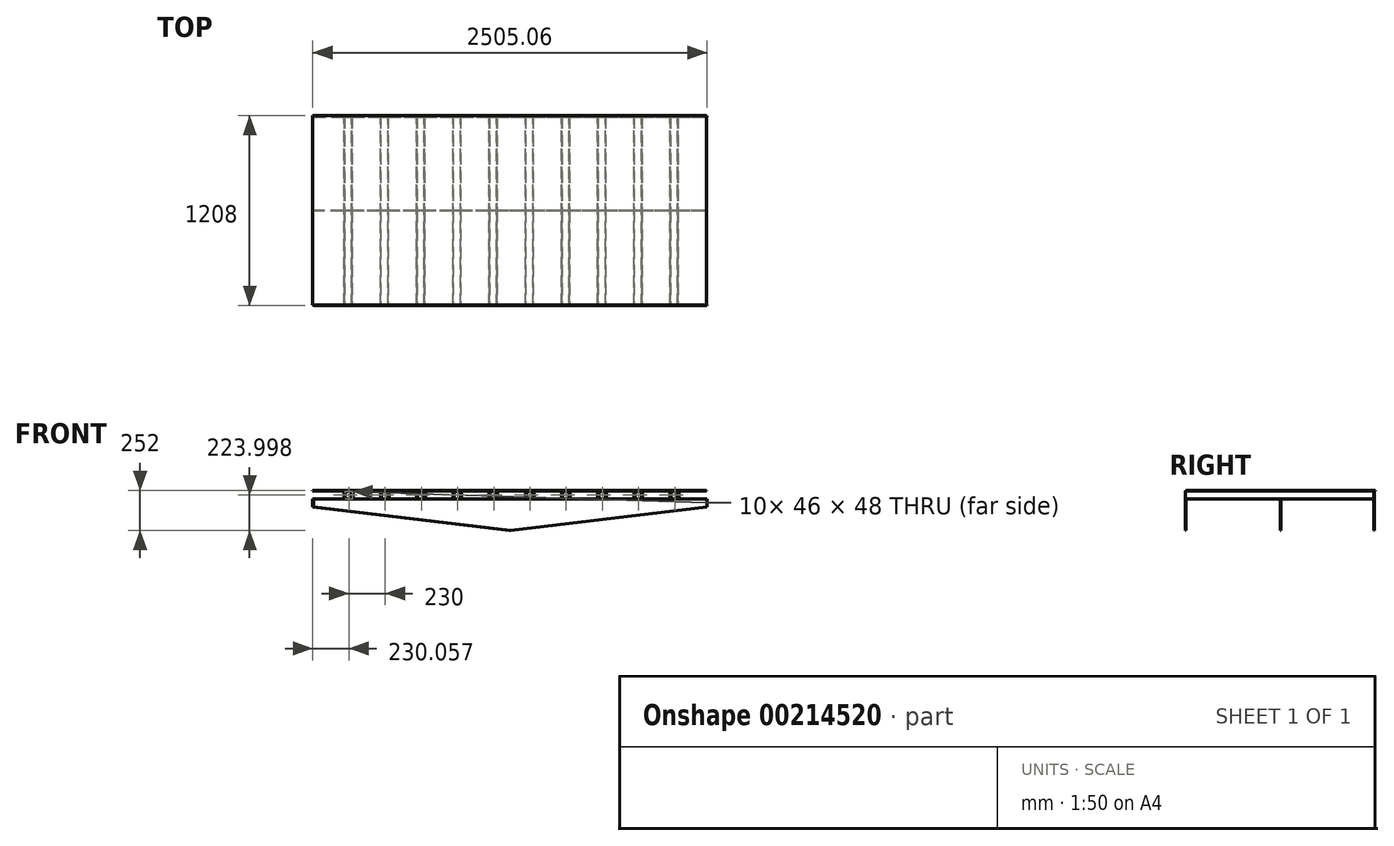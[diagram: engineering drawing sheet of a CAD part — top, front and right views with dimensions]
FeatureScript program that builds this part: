
annotation { "Feature Type Name" : "Feature", "Feature Type Description" : "" }
export const myFeature = defineFeature(function(context is Context, id is Id, definition is map)
    precondition{}
    {
        {
            var Q0;
            Q0=qCreatedBy(makeId("Front.planeOp"),FACE);
            var sketch = newSketch(context, id + "F0", { "sketchPlane" : qUnion([Q0])});
            skLineSegment(sketch, "E0.bottom", {"start": v(-1251.25, 23.13) * mm, "end": v(1248.75, 23.13) * mm});
            skLineSegment(sketch, "E1.bottom", {"start": v(-1051.25, 73.13) * mm, "end": v(-1001.25, 73.13) * mm});
            skLineSegment(sketch, "E1.left", {"start": v(-1001.25, 73.13) * mm, "end": v(-1001.25, 23.13) * mm});
            skLineSegment(sketch, "E1.right", {"start": v(-1051.25, 73.13) * mm, "end": v(-1051.25, 23.13) * mm});
            skLineSegment(sketch, "E2", {"start": v(-1251.25, 23.13) * mm, "end": v(-1251.25, -26.87) * mm});
            skLineSegment(sketch, "E3", {"start": v(-1251.25, -26.87) * mm, "end": v(0, -176.87) * mm});
            skLineSegment(sketch, "E4", {"start": v(0, -176.87) * mm, "end": v(1248.75, -26.87) * mm});
            skLineSegment(sketch, "E5", {"start": v(1248.75, -26.87) * mm, "end": v(1248.75, 23.13) * mm});
            skLineSegment(sketch, "E6", {"start": v(-1003.25, 23.13) * mm, "end": v(-1003.25, 71.13) * mm});
            skLineSegment(sketch, "E7", {"start": v(-1003.25, 71.13) * mm, "end": v(-1049.25, 71.13) * mm});
            skLineSegment(sketch, "E8", {"start": v(-1049.25, 71.13) * mm, "end": v(-1049.25, 23.13) * mm});
            skLineSegment(sketch, "E9.1.0.0", {"start": v(-821.25, 73.13) * mm, "end": v(-821.25, 23.13) * mm});
            skLineSegment(sketch, "E9.1.0.1", {"start": v(-773.25, 23.13) * mm, "end": v(-773.25, 71.13) * mm});
            skLineSegment(sketch, "E9.1.0.2", {"start": v(-821.25, 73.13) * mm, "end": v(-771.25, 73.13) * mm});
            skLineSegment(sketch, "E9.1.0.3", {"start": v(-771.25, 73.13) * mm, "end": v(-771.25, 23.13) * mm});
            skLineSegment(sketch, "E9.1.0.4", {"start": v(-773.25, 71.13) * mm, "end": v(-819.25, 71.13) * mm});
            skLineSegment(sketch, "E9.1.0.5", {"start": v(-819.25, 71.13) * mm, "end": v(-819.25, 23.13) * mm});
            skLineSegment(sketch, "E9.2.0.0", {"start": v(-591.25, 73.13) * mm, "end": v(-591.25, 23.13) * mm});
            skLineSegment(sketch, "E9.2.0.1", {"start": v(-543.25, 23.13) * mm, "end": v(-543.25, 71.13) * mm});
            skLineSegment(sketch, "E9.2.0.2", {"start": v(-591.25, 73.13) * mm, "end": v(-541.25, 73.13) * mm});
            skLineSegment(sketch, "E9.2.0.3", {"start": v(-541.25, 73.13) * mm, "end": v(-541.25, 23.13) * mm});
            skLineSegment(sketch, "E9.2.0.4", {"start": v(-543.25, 71.13) * mm, "end": v(-589.25, 71.13) * mm});
            skLineSegment(sketch, "E9.2.0.5", {"start": v(-589.25, 71.13) * mm, "end": v(-589.25, 23.13) * mm});
            skLineSegment(sketch, "E9.3.0.0", {"start": v(-361.25, 73.13) * mm, "end": v(-361.25, 23.13) * mm});
            skLineSegment(sketch, "E9.3.0.1", {"start": v(-313.25, 23.13) * mm, "end": v(-313.25, 71.13) * mm});
            skLineSegment(sketch, "E9.3.0.2", {"start": v(-361.25, 73.13) * mm, "end": v(-311.25, 73.13) * mm});
            skLineSegment(sketch, "E9.3.0.3", {"start": v(-311.25, 73.13) * mm, "end": v(-311.25, 23.13) * mm});
            skLineSegment(sketch, "E9.3.0.4", {"start": v(-313.25, 71.13) * mm, "end": v(-359.25, 71.13) * mm});
            skLineSegment(sketch, "E9.3.0.5", {"start": v(-359.25, 71.13) * mm, "end": v(-359.25, 23.13) * mm});
            skLineSegment(sketch, "E9.4.0.0", {"start": v(-131.25, 73.13) * mm, "end": v(-131.25, 23.13) * mm});
            skLineSegment(sketch, "E9.4.0.1", {"start": v(-83.25, 23.13) * mm, "end": v(-83.25, 71.13) * mm});
            skLineSegment(sketch, "E9.4.0.2", {"start": v(-131.25, 73.13) * mm, "end": v(-81.25, 73.13) * mm});
            skLineSegment(sketch, "E9.4.0.3", {"start": v(-81.25, 73.13) * mm, "end": v(-81.25, 23.13) * mm});
            skLineSegment(sketch, "E9.4.0.4", {"start": v(-83.25, 71.13) * mm, "end": v(-129.25, 71.13) * mm});
            skLineSegment(sketch, "E9.4.0.5", {"start": v(-129.25, 71.13) * mm, "end": v(-129.25, 23.13) * mm});
            skLineSegment(sketch, "E9.5.0.0", {"start": v(98.75, 73.13) * mm, "end": v(98.75, 23.13) * mm});
            skLineSegment(sketch, "E9.5.0.1", {"start": v(146.75, 23.13) * mm, "end": v(146.75, 71.13) * mm});
            skLineSegment(sketch, "E9.5.0.2", {"start": v(98.75, 73.13) * mm, "end": v(148.75, 73.13) * mm});
            skLineSegment(sketch, "E9.5.0.3", {"start": v(148.75, 73.13) * mm, "end": v(148.75, 23.13) * mm});
            skLineSegment(sketch, "E9.5.0.4", {"start": v(146.75, 71.13) * mm, "end": v(100.75, 71.13) * mm});
            skLineSegment(sketch, "E9.5.0.5", {"start": v(100.75, 71.13) * mm, "end": v(100.75, 23.13) * mm});
            skLineSegment(sketch, "E9.6.0.0", {"start": v(328.75, 73.13) * mm, "end": v(328.75, 23.13) * mm});
            skLineSegment(sketch, "E9.6.0.1", {"start": v(376.75, 23.13) * mm, "end": v(376.75, 71.13) * mm});
            skLineSegment(sketch, "E9.6.0.2", {"start": v(328.75, 73.13) * mm, "end": v(378.75, 73.13) * mm});
            skLineSegment(sketch, "E9.6.0.3", {"start": v(378.75, 73.13) * mm, "end": v(378.75, 23.13) * mm});
            skLineSegment(sketch, "E9.6.0.4", {"start": v(376.75, 71.13) * mm, "end": v(330.75, 71.13) * mm});
            skLineSegment(sketch, "E9.6.0.5", {"start": v(330.75, 71.13) * mm, "end": v(330.75, 23.13) * mm});
            skLineSegment(sketch, "E9.7.0.0", {"start": v(558.75, 73.13) * mm, "end": v(558.75, 23.13) * mm});
            skLineSegment(sketch, "E9.7.0.1", {"start": v(606.75, 23.13) * mm, "end": v(606.75, 71.13) * mm});
            skLineSegment(sketch, "E9.7.0.2", {"start": v(558.75, 73.13) * mm, "end": v(608.75, 73.13) * mm});
            skLineSegment(sketch, "E9.7.0.3", {"start": v(608.75, 73.13) * mm, "end": v(608.75, 23.13) * mm});
            skLineSegment(sketch, "E9.7.0.4", {"start": v(606.75, 71.13) * mm, "end": v(560.75, 71.13) * mm});
            skLineSegment(sketch, "E9.7.0.5", {"start": v(560.75, 71.13) * mm, "end": v(560.75, 23.13) * mm});
            skLineSegment(sketch, "E9.8.0.0", {"start": v(788.75, 73.13) * mm, "end": v(788.75, 23.13) * mm});
            skLineSegment(sketch, "E9.8.0.1", {"start": v(836.75, 23.13) * mm, "end": v(836.75, 71.13) * mm});
            skLineSegment(sketch, "E9.8.0.2", {"start": v(788.75, 73.13) * mm, "end": v(838.75, 73.13) * mm});
            skLineSegment(sketch, "E9.8.0.3", {"start": v(838.75, 73.13) * mm, "end": v(838.75, 23.13) * mm});
            skLineSegment(sketch, "E9.8.0.4", {"start": v(836.75, 71.13) * mm, "end": v(790.75, 71.13) * mm});
            skLineSegment(sketch, "E9.8.0.5", {"start": v(790.75, 71.13) * mm, "end": v(790.75, 23.13) * mm});
            skLineSegment(sketch, "E9.9.0.0", {"start": v(1018.75, 73.13) * mm, "end": v(1018.75, 23.13) * mm});
            skLineSegment(sketch, "E9.9.0.1", {"start": v(1066.75, 23.13) * mm, "end": v(1066.75, 71.13) * mm});
            skLineSegment(sketch, "E9.9.0.2", {"start": v(1018.75, 73.13) * mm, "end": v(1068.75, 73.13) * mm});
            skLineSegment(sketch, "E9.9.0.3", {"start": v(1068.75, 73.13) * mm, "end": v(1068.75, 23.13) * mm});
            skLineSegment(sketch, "E9.9.0.4", {"start": v(1066.75, 71.13) * mm, "end": v(1020.75, 71.13) * mm});
            skLineSegment(sketch, "E9.9.0.5", {"start": v(1020.75, 71.13) * mm, "end": v(1020.75, 23.13) * mm});
            skLineSegment(sketch, "E9.direction1", {"start": v(-1051.25, 23.13) * mm, "end": v(-821.25, 23.13) * mm, "construction": true});
            skSolve(sketch);
        }
        {
            var Q0;
            Q0 = qSketchRegion(id + "F0", true);
            extrude(context, id + "F1", {"entities" : qUnion([Q0]), "depth" : 5 * mm, "offsetDistance" : 25 * mm});
        }
        {
            var Q0;
            Q0=makeQuery(id+"F1.opExtrude","SWEPT_FACE",FACE,{"disambiguationData":[OSD([sQuery(id+"F0.wireOp",EDGE,"E1.bottom")])]});
            var sketch = newSketch(context, id + "F2", { "sketchPlane" : qUnion([Q0])});
            skLineSegment(sketch, "E10.bottom", {"start": v(-1251.25, 600) * mm, "end": v(1248.75, 600) * mm});
            skLineSegment(sketch, "E10.top", {"start": v(-1251.25, -605) * mm, "end": v(1248.75, -605) * mm});
            skLineSegment(sketch, "E10.left", {"start": v(-1251.25, 600) * mm, "end": v(-1251.25, -605) * mm});
            skLineSegment(sketch, "E10.right", {"start": v(1248.75, 600) * mm, "end": v(1248.75, -605) * mm});
            skSolve(sketch);
        }
        {
            var Q0;
            Q0 = qSketchRegion(id + "F2", true);
            extrude(context, id + "F3", {"entities" : qUnion([Q0]), "operationType" : NewBodyOperationType.ADD, "depth" : 2 * mm, "offsetDistance" : 25 * mm});
        }
        {
            var Q0;
            Q0=makeQuery(id+"F1.opExtrude","CAP_FACE",FACE,{"disambiguationData":[OSD([sQuery(id+"F0.wireOp",EDGE,"E0.bottom"),sQuery(id+"F0.wireOp",EDGE,"E1.bottom"),sQuery(id+"F0.wireOp",EDGE,"E1.left"),sQuery(id+"F0.wireOp",EDGE,"E1.right"),sQuery(id+"F0.wireOp",EDGE,"E2"),sQuery(id+"F0.wireOp",EDGE,"E3"),sQuery(id+"F0.wireOp",EDGE,"E4"),sQuery(id+"F0.wireOp",EDGE,"E5"),sQuery(id+"F0.wireOp",EDGE,"E6"),sQuery(id+"F0.wireOp",EDGE,"E7"),sQuery(id+"F0.wireOp",EDGE,"E8"),sQuery(id+"F0.wireOp",EDGE,"E9.1.0.0"),sQuery(id+"F0.wireOp",EDGE,"E9.1.0.1"),sQuery(id+"F0.wireOp",EDGE,"E9.1.0.2"),sQuery(id+"F0.wireOp",EDGE,"E9.1.0.3"),sQuery(id+"F0.wireOp",EDGE,"E9.1.0.4"),sQuery(id+"F0.wireOp",EDGE,"E9.1.0.5"),sQuery(id+"F0.wireOp",EDGE,"E9.2.0.0"),sQuery(id+"F0.wireOp",EDGE,"E9.2.0.1"),sQuery(id+"F0.wireOp",EDGE,"E9.2.0.2"),sQuery(id+"F0.wireOp",EDGE,"E9.2.0.3"),sQuery(id+"F0.wireOp",EDGE,"E9.2.0.4"),sQuery(id+"F0.wireOp",EDGE,"E9.2.0.5"),sQuery(id+"F0.wireOp",EDGE,"E9.3.0.0"),sQuery(id+"F0.wireOp",EDGE,"E9.3.0.1"),sQuery(id+"F0.wireOp",EDGE,"E9.3.0.2"),sQuery(id+"F0.wireOp",EDGE,"E9.3.0.3"),sQuery(id+"F0.wireOp",EDGE,"E9.3.0.4"),sQuery(id+"F0.wireOp",EDGE,"E9.3.0.5"),sQuery(id+"F0.wireOp",EDGE,"E9.4.0.0"),sQuery(id+"F0.wireOp",EDGE,"E9.4.0.1"),sQuery(id+"F0.wireOp",EDGE,"E9.4.0.2"),sQuery(id+"F0.wireOp",EDGE,"E9.4.0.3"),sQuery(id+"F0.wireOp",EDGE,"E9.4.0.4"),sQuery(id+"F0.wireOp",EDGE,"E9.4.0.5"),sQuery(id+"F0.wireOp",EDGE,"E9.5.0.0"),sQuery(id+"F0.wireOp",EDGE,"E9.5.0.1"),sQuery(id+"F0.wireOp",EDGE,"E9.5.0.2"),sQuery(id+"F0.wireOp",EDGE,"E9.5.0.3"),sQuery(id+"F0.wireOp",EDGE,"E9.5.0.4"),sQuery(id+"F0.wireOp",EDGE,"E9.5.0.5"),sQuery(id+"F0.wireOp",EDGE,"E9.6.0.0"),sQuery(id+"F0.wireOp",EDGE,"E9.6.0.1"),sQuery(id+"F0.wireOp",EDGE,"E9.6.0.2"),sQuery(id+"F0.wireOp",EDGE,"E9.6.0.3"),sQuery(id+"F0.wireOp",EDGE,"E9.6.0.4"),sQuery(id+"F0.wireOp",EDGE,"E9.6.0.5"),sQuery(id+"F0.wireOp",EDGE,"E9.7.0.0"),sQuery(id+"F0.wireOp",EDGE,"E9.7.0.1"),sQuery(id+"F0.wireOp",EDGE,"E9.7.0.2"),sQuery(id+"F0.wireOp",EDGE,"E9.7.0.3"),sQuery(id+"F0.wireOp",EDGE,"E9.7.0.4"),sQuery(id+"F0.wireOp",EDGE,"E9.7.0.5"),sQuery(id+"F0.wireOp",EDGE,"E9.8.0.0"),sQuery(id+"F0.wireOp",EDGE,"E9.8.0.1"),sQuery(id+"F0.wireOp",EDGE,"E9.8.0.2"),sQuery(id+"F0.wireOp",EDGE,"E9.8.0.3"),sQuery(id+"F0.wireOp",EDGE,"E9.8.0.4"),sQuery(id+"F0.wireOp",EDGE,"E9.8.0.5"),sQuery(id+"F0.wireOp",EDGE,"E9.9.0.0"),sQuery(id+"F0.wireOp",EDGE,"E9.9.0.1"),sQuery(id+"F0.wireOp",EDGE,"E9.9.0.2"),sQuery(id+"F0.wireOp",EDGE,"E9.9.0.3"),sQuery(id+"F0.wireOp",EDGE,"E9.9.0.4"),sQuery(id+"F0.wireOp",EDGE,"E9.9.0.5")])],"isStart":false});
            var sketch = newSketch(context, id + "F4", { "sketchPlane" : qUnion([Q0])});
            skSolve(sketch);
        }
        {
            var Q0;
            {var subQ21=sQuery(id+"F0.wireOp",EDGE,"E1.left");Q0=makeQuery(id+"F4.imprint","IMPRINT",FACE,{"disambiguationData":[TD([[makeQuery(id+"F4.imprint","IMPRINT",EDGE,{"derivedFrom":makeQuery(id+"F1.opExtrude","CAP_EDGE",EDGE,{"disambiguationData":[OSD([subQ21])],"isStart":false})}),-1.0]])]});}
            cPlane(context, id + "F5", {"entities" : qUnion([Q0]), "cplaneType" : CPlaneType.OFFSET, "offset" : 600 * mm, "width" : 150 * mm, "height" : 150 * mm});
        }
        {
            var Q0;
            Q0=qCreatedBy(id+"F5.planeOp",FACE);
            var sketch = newSketch(context, id + "F6", { "sketchPlane" : qUnion([Q0])});
            skLineSegment(sketch, "E11.bottom", {"start": v(-1246.2, 23.13) * mm, "end": v(1253.8, 23.13) * mm});
            skLineSegment(sketch, "E12.bottom", {"start": v(-1051.25, 73.13) * mm, "end": v(-1001.25, 73.13) * mm});
            skLineSegment(sketch, "E12.left", {"start": v(-1001.25, 73.13) * mm, "end": v(-1001.25, 23.13) * mm});
            skLineSegment(sketch, "E12.right", {"start": v(-1051.25, 73.13) * mm, "end": v(-1051.25, 23.13) * mm});
            skLineSegment(sketch, "E13", {"start": v(-1246.2, 23.13) * mm, "end": v(-1246.2, -26.87) * mm});
            skLineSegment(sketch, "E14", {"start": v(-1246.2, -26.87) * mm, "end": v(5.06, -176.87) * mm});
            skLineSegment(sketch, "E15", {"start": v(5.06, -176.87) * mm, "end": v(1253.8, -26.87) * mm});
            skLineSegment(sketch, "E16", {"start": v(1253.8, -26.87) * mm, "end": v(1253.8, 23.13) * mm});
            skLineSegment(sketch, "E17", {"start": v(-1003.25, 23.13) * mm, "end": v(-1003.25, 71.13) * mm});
            skLineSegment(sketch, "E18", {"start": v(-1003.25, 71.13) * mm, "end": v(-1049.25, 71.13) * mm});
            skLineSegment(sketch, "E19", {"start": v(-1049.25, 71.13) * mm, "end": v(-1049.25, 23.13) * mm});
            skLineSegment(sketch, "E20.1.0.0", {"start": v(-821.25, 73.13) * mm, "end": v(-821.25, 23.13) * mm});
            skLineSegment(sketch, "E20.1.0.1", {"start": v(-773.25, 23.13) * mm, "end": v(-773.25, 71.13) * mm});
            skLineSegment(sketch, "E20.1.0.2", {"start": v(-821.25, 73.13) * mm, "end": v(-771.25, 73.13) * mm});
            skLineSegment(sketch, "E20.1.0.3", {"start": v(-771.25, 73.13) * mm, "end": v(-771.25, 23.13) * mm});
            skLineSegment(sketch, "E20.1.0.4", {"start": v(-773.25, 71.13) * mm, "end": v(-819.25, 71.13) * mm});
            skLineSegment(sketch, "E20.1.0.5", {"start": v(-819.25, 71.13) * mm, "end": v(-819.25, 23.13) * mm});
            skLineSegment(sketch, "E20.2.0.0", {"start": v(-591.25, 73.13) * mm, "end": v(-591.25, 23.13) * mm});
            skLineSegment(sketch, "E20.2.0.1", {"start": v(-543.25, 23.13) * mm, "end": v(-543.25, 71.13) * mm});
            skLineSegment(sketch, "E20.2.0.2", {"start": v(-591.25, 73.13) * mm, "end": v(-541.25, 73.13) * mm});
            skLineSegment(sketch, "E20.2.0.3", {"start": v(-541.25, 73.13) * mm, "end": v(-541.25, 23.13) * mm});
            skLineSegment(sketch, "E20.2.0.4", {"start": v(-543.25, 71.13) * mm, "end": v(-589.25, 71.13) * mm});
            skLineSegment(sketch, "E20.2.0.5", {"start": v(-589.25, 71.13) * mm, "end": v(-589.25, 23.13) * mm});
            skLineSegment(sketch, "E20.3.0.0", {"start": v(-361.25, 73.13) * mm, "end": v(-361.25, 23.13) * mm});
            skLineSegment(sketch, "E20.3.0.1", {"start": v(-313.25, 23.13) * mm, "end": v(-313.25, 71.13) * mm});
            skLineSegment(sketch, "E20.3.0.2", {"start": v(-361.25, 73.13) * mm, "end": v(-311.25, 73.13) * mm});
            skLineSegment(sketch, "E20.3.0.3", {"start": v(-311.25, 73.13) * mm, "end": v(-311.25, 23.13) * mm});
            skLineSegment(sketch, "E20.3.0.4", {"start": v(-313.25, 71.13) * mm, "end": v(-359.25, 71.13) * mm});
            skLineSegment(sketch, "E20.3.0.5", {"start": v(-359.25, 71.13) * mm, "end": v(-359.25, 23.13) * mm});
            skLineSegment(sketch, "E20.4.0.0", {"start": v(-131.25, 73.13) * mm, "end": v(-131.25, 23.13) * mm});
            skLineSegment(sketch, "E20.4.0.1", {"start": v(-83.25, 23.13) * mm, "end": v(-83.25, 71.13) * mm});
            skLineSegment(sketch, "E20.4.0.2", {"start": v(-131.25, 73.13) * mm, "end": v(-81.25, 73.13) * mm});
            skLineSegment(sketch, "E20.4.0.3", {"start": v(-81.25, 73.13) * mm, "end": v(-81.25, 23.13) * mm});
            skLineSegment(sketch, "E20.4.0.4", {"start": v(-83.25, 71.13) * mm, "end": v(-129.25, 71.13) * mm});
            skLineSegment(sketch, "E20.4.0.5", {"start": v(-129.25, 71.13) * mm, "end": v(-129.25, 23.13) * mm});
            skLineSegment(sketch, "E20.5.0.0", {"start": v(98.75, 73.13) * mm, "end": v(98.75, 23.13) * mm});
            skLineSegment(sketch, "E20.5.0.1", {"start": v(146.75, 23.13) * mm, "end": v(146.75, 71.13) * mm});
            skLineSegment(sketch, "E20.5.0.2", {"start": v(98.75, 73.13) * mm, "end": v(148.75, 73.13) * mm});
            skLineSegment(sketch, "E20.5.0.3", {"start": v(148.75, 73.13) * mm, "end": v(148.75, 23.13) * mm});
            skLineSegment(sketch, "E20.5.0.4", {"start": v(146.75, 71.13) * mm, "end": v(100.75, 71.13) * mm});
            skLineSegment(sketch, "E20.5.0.5", {"start": v(100.75, 71.13) * mm, "end": v(100.75, 23.13) * mm});
            skLineSegment(sketch, "E20.6.0.0", {"start": v(328.75, 73.13) * mm, "end": v(328.75, 23.13) * mm});
            skLineSegment(sketch, "E20.6.0.1", {"start": v(376.75, 23.13) * mm, "end": v(376.75, 71.13) * mm});
            skLineSegment(sketch, "E20.6.0.2", {"start": v(328.75, 73.13) * mm, "end": v(378.75, 73.13) * mm});
            skLineSegment(sketch, "E20.6.0.3", {"start": v(378.75, 73.13) * mm, "end": v(378.75, 23.13) * mm});
            skLineSegment(sketch, "E20.6.0.4", {"start": v(376.75, 71.13) * mm, "end": v(330.75, 71.13) * mm});
            skLineSegment(sketch, "E20.6.0.5", {"start": v(330.75, 71.13) * mm, "end": v(330.75, 23.13) * mm});
            skLineSegment(sketch, "E20.7.0.0", {"start": v(558.75, 73.13) * mm, "end": v(558.75, 23.13) * mm});
            skLineSegment(sketch, "E20.7.0.1", {"start": v(606.75, 23.13) * mm, "end": v(606.75, 71.13) * mm});
            skLineSegment(sketch, "E20.7.0.2", {"start": v(558.75, 73.13) * mm, "end": v(608.75, 73.13) * mm});
            skLineSegment(sketch, "E20.7.0.3", {"start": v(608.75, 73.13) * mm, "end": v(608.75, 23.13) * mm});
            skLineSegment(sketch, "E20.7.0.4", {"start": v(606.75, 71.13) * mm, "end": v(560.75, 71.13) * mm});
            skLineSegment(sketch, "E20.7.0.5", {"start": v(560.75, 71.13) * mm, "end": v(560.75, 23.13) * mm});
            skLineSegment(sketch, "E20.8.0.0", {"start": v(788.75, 73.13) * mm, "end": v(788.75, 23.13) * mm});
            skLineSegment(sketch, "E20.8.0.1", {"start": v(836.75, 23.13) * mm, "end": v(836.75, 71.13) * mm});
            skLineSegment(sketch, "E20.8.0.2", {"start": v(788.75, 73.13) * mm, "end": v(838.75, 73.13) * mm});
            skLineSegment(sketch, "E20.8.0.3", {"start": v(838.75, 73.13) * mm, "end": v(838.75, 23.13) * mm});
            skLineSegment(sketch, "E20.8.0.4", {"start": v(836.75, 71.13) * mm, "end": v(790.75, 71.13) * mm});
            skLineSegment(sketch, "E20.8.0.5", {"start": v(790.75, 71.13) * mm, "end": v(790.75, 23.13) * mm});
            skLineSegment(sketch, "E20.9.0.0", {"start": v(1018.75, 73.13) * mm, "end": v(1018.75, 23.13) * mm});
            skLineSegment(sketch, "E20.9.0.1", {"start": v(1066.75, 23.13) * mm, "end": v(1066.75, 71.13) * mm});
            skLineSegment(sketch, "E20.9.0.2", {"start": v(1018.75, 73.13) * mm, "end": v(1068.75, 73.13) * mm});
            skLineSegment(sketch, "E20.9.0.3", {"start": v(1068.75, 73.13) * mm, "end": v(1068.75, 23.13) * mm});
            skLineSegment(sketch, "E20.9.0.4", {"start": v(1066.75, 71.13) * mm, "end": v(1020.75, 71.13) * mm});
            skLineSegment(sketch, "E20.9.0.5", {"start": v(1020.75, 71.13) * mm, "end": v(1020.75, 23.13) * mm});
            skLineSegment(sketch, "E20.direction1", {"start": v(-1051.25, 23.13) * mm, "end": v(-821.25, 23.13) * mm, "construction": true});
            skSolve(sketch);
        }
        {
            var Q0;
            Q0 = qSketchRegion(id + "F6", true);
            extrude(context, id + "F7", {"entities" : qUnion([Q0]), "depth" : 3 * mm, "offsetDistance" : 25 * mm});
        }
        {
            var Q0;
            Q0=makeQuery(id+"F7.opExtrude","CAP_FACE",FACE,{"disambiguationData":[OSD([sQuery(id+"F6.wireOp",EDGE,"E11.bottom"),sQuery(id+"F6.wireOp",EDGE,"E12.bottom"),sQuery(id+"F6.wireOp",EDGE,"E12.left"),sQuery(id+"F6.wireOp",EDGE,"E12.right"),sQuery(id+"F6.wireOp",EDGE,"E13"),sQuery(id+"F6.wireOp",EDGE,"E14"),sQuery(id+"F6.wireOp",EDGE,"E15"),sQuery(id+"F6.wireOp",EDGE,"E16"),sQuery(id+"F6.wireOp",EDGE,"E17"),sQuery(id+"F6.wireOp",EDGE,"E18"),sQuery(id+"F6.wireOp",EDGE,"E19"),sQuery(id+"F6.wireOp",EDGE,"E20.1.0.0"),sQuery(id+"F6.wireOp",EDGE,"E20.1.0.1"),sQuery(id+"F6.wireOp",EDGE,"E20.1.0.2"),sQuery(id+"F6.wireOp",EDGE,"E20.1.0.3"),sQuery(id+"F6.wireOp",EDGE,"E20.1.0.4"),sQuery(id+"F6.wireOp",EDGE,"E20.1.0.5"),sQuery(id+"F6.wireOp",EDGE,"E20.2.0.0"),sQuery(id+"F6.wireOp",EDGE,"E20.2.0.1"),sQuery(id+"F6.wireOp",EDGE,"E20.2.0.2"),sQuery(id+"F6.wireOp",EDGE,"E20.2.0.3"),sQuery(id+"F6.wireOp",EDGE,"E20.2.0.4"),sQuery(id+"F6.wireOp",EDGE,"E20.2.0.5"),sQuery(id+"F6.wireOp",EDGE,"E20.3.0.0"),sQuery(id+"F6.wireOp",EDGE,"E20.3.0.1"),sQuery(id+"F6.wireOp",EDGE,"E20.3.0.2"),sQuery(id+"F6.wireOp",EDGE,"E20.3.0.3"),sQuery(id+"F6.wireOp",EDGE,"E20.3.0.4"),sQuery(id+"F6.wireOp",EDGE,"E20.3.0.5"),sQuery(id+"F6.wireOp",EDGE,"E20.4.0.0"),sQuery(id+"F6.wireOp",EDGE,"E20.4.0.1"),sQuery(id+"F6.wireOp",EDGE,"E20.4.0.2"),sQuery(id+"F6.wireOp",EDGE,"E20.4.0.3"),sQuery(id+"F6.wireOp",EDGE,"E20.4.0.4"),sQuery(id+"F6.wireOp",EDGE,"E20.4.0.5"),sQuery(id+"F6.wireOp",EDGE,"E20.5.0.0"),sQuery(id+"F6.wireOp",EDGE,"E20.5.0.1"),sQuery(id+"F6.wireOp",EDGE,"E20.5.0.2"),sQuery(id+"F6.wireOp",EDGE,"E20.5.0.3"),sQuery(id+"F6.wireOp",EDGE,"E20.5.0.4"),sQuery(id+"F6.wireOp",EDGE,"E20.5.0.5"),sQuery(id+"F6.wireOp",EDGE,"E20.6.0.0"),sQuery(id+"F6.wireOp",EDGE,"E20.6.0.1"),sQuery(id+"F6.wireOp",EDGE,"E20.6.0.2"),sQuery(id+"F6.wireOp",EDGE,"E20.6.0.3"),sQuery(id+"F6.wireOp",EDGE,"E20.6.0.4"),sQuery(id+"F6.wireOp",EDGE,"E20.6.0.5"),sQuery(id+"F6.wireOp",EDGE,"E20.7.0.0"),sQuery(id+"F6.wireOp",EDGE,"E20.7.0.1"),sQuery(id+"F6.wireOp",EDGE,"E20.7.0.2"),sQuery(id+"F6.wireOp",EDGE,"E20.7.0.3"),sQuery(id+"F6.wireOp",EDGE,"E20.7.0.4"),sQuery(id+"F6.wireOp",EDGE,"E20.7.0.5"),sQuery(id+"F6.wireOp",EDGE,"E20.8.0.0"),sQuery(id+"F6.wireOp",EDGE,"E20.8.0.1"),sQuery(id+"F6.wireOp",EDGE,"E20.8.0.2"),sQuery(id+"F6.wireOp",EDGE,"E20.8.0.3"),sQuery(id+"F6.wireOp",EDGE,"E20.8.0.4"),sQuery(id+"F6.wireOp",EDGE,"E20.8.0.5"),sQuery(id+"F6.wireOp",EDGE,"E20.9.0.0"),sQuery(id+"F6.wireOp",EDGE,"E20.9.0.1"),sQuery(id+"F6.wireOp",EDGE,"E20.9.0.2"),sQuery(id+"F6.wireOp",EDGE,"E20.9.0.3"),sQuery(id+"F6.wireOp",EDGE,"E20.9.0.4"),sQuery(id+"F6.wireOp",EDGE,"E20.9.0.5")])],"isStart":false});
            var sketch = newSketch(context, id + "F8", { "sketchPlane" : qUnion([Q0])});
            skLineSegment(sketch, "E21", {"start": v(-1051.25, 23.13) * mm, "end": v(-1051.25, 73.13) * mm});
            skLineSegment(sketch, "E22", {"start": v(-1051.25, 73.13) * mm, "end": v(-1001.25, 73.13) * mm});
            skLineSegment(sketch, "E23", {"start": v(-1001.25, 73.13) * mm, "end": v(-1001.25, 23.13) * mm});
            skLineSegment(sketch, "E24", {"start": v(-1001.25, 23.13) * mm, "end": v(-1003.25, 23.13) * mm});
            skLineSegment(sketch, "E25", {"start": v(-1003.25, 23.13) * mm, "end": v(-1003.25, 71.13) * mm});
            skLineSegment(sketch, "E26", {"start": v(-1003.25, 71.13) * mm, "end": v(-1049.25, 71.13) * mm});
            skLineSegment(sketch, "E27", {"start": v(-1049.25, 71.13) * mm, "end": v(-1049.25, 23.13) * mm});
            skLineSegment(sketch, "E28", {"start": v(-1049.25, 23.13) * mm, "end": v(-1051.25, 23.13) * mm});
            skLineSegment(sketch, "E29.1.0.0", {"start": v(-773.25, 23.13) * mm, "end": v(-773.25, 71.13) * mm});
            skLineSegment(sketch, "E29.1.0.1", {"start": v(-821.25, 23.13) * mm, "end": v(-821.25, 73.13) * mm});
            skLineSegment(sketch, "E29.1.0.2", {"start": v(-771.25, 73.13) * mm, "end": v(-771.25, 23.13) * mm});
            skLineSegment(sketch, "E29.1.0.3", {"start": v(-773.25, 71.13) * mm, "end": v(-819.25, 71.13) * mm});
            skLineSegment(sketch, "E29.1.0.4", {"start": v(-819.25, 71.13) * mm, "end": v(-819.25, 23.13) * mm});
            skLineSegment(sketch, "E29.1.0.5", {"start": v(-821.25, 73.13) * mm, "end": v(-771.25, 73.13) * mm});
            skLineSegment(sketch, "E29.1.0.6", {"start": v(-771.25, 23.13) * mm, "end": v(-773.25, 23.13) * mm});
            skLineSegment(sketch, "E29.1.0.7", {"start": v(-819.25, 23.13) * mm, "end": v(-821.25, 23.13) * mm});
            skLineSegment(sketch, "E29.2.0.0", {"start": v(-543.25, 23.13) * mm, "end": v(-543.25, 71.13) * mm});
            skLineSegment(sketch, "E29.2.0.1", {"start": v(-591.25, 23.13) * mm, "end": v(-591.25, 73.13) * mm});
            skLineSegment(sketch, "E29.2.0.2", {"start": v(-541.25, 73.13) * mm, "end": v(-541.25, 23.13) * mm});
            skLineSegment(sketch, "E29.2.0.3", {"start": v(-543.25, 71.13) * mm, "end": v(-589.25, 71.13) * mm});
            skLineSegment(sketch, "E29.2.0.4", {"start": v(-589.25, 71.13) * mm, "end": v(-589.25, 23.13) * mm});
            skLineSegment(sketch, "E29.2.0.5", {"start": v(-591.25, 73.13) * mm, "end": v(-541.25, 73.13) * mm});
            skLineSegment(sketch, "E29.2.0.6", {"start": v(-541.25, 23.13) * mm, "end": v(-543.25, 23.13) * mm});
            skLineSegment(sketch, "E29.2.0.7", {"start": v(-589.25, 23.13) * mm, "end": v(-591.25, 23.13) * mm});
            skLineSegment(sketch, "E29.3.0.0", {"start": v(-313.25, 23.13) * mm, "end": v(-313.25, 71.13) * mm});
            skLineSegment(sketch, "E29.3.0.1", {"start": v(-361.25, 23.13) * mm, "end": v(-361.25, 73.13) * mm});
            skLineSegment(sketch, "E29.3.0.2", {"start": v(-311.25, 73.13) * mm, "end": v(-311.25, 23.13) * mm});
            skLineSegment(sketch, "E29.3.0.3", {"start": v(-313.25, 71.13) * mm, "end": v(-359.25, 71.13) * mm});
            skLineSegment(sketch, "E29.3.0.4", {"start": v(-359.25, 71.13) * mm, "end": v(-359.25, 23.13) * mm});
            skLineSegment(sketch, "E29.3.0.5", {"start": v(-361.25, 73.13) * mm, "end": v(-311.25, 73.13) * mm});
            skLineSegment(sketch, "E29.3.0.6", {"start": v(-311.25, 23.13) * mm, "end": v(-313.25, 23.13) * mm});
            skLineSegment(sketch, "E29.3.0.7", {"start": v(-359.25, 23.13) * mm, "end": v(-361.25, 23.13) * mm});
            skLineSegment(sketch, "E29.4.0.0", {"start": v(-83.25, 23.13) * mm, "end": v(-83.25, 71.13) * mm});
            skLineSegment(sketch, "E29.4.0.1", {"start": v(-131.25, 23.13) * mm, "end": v(-131.25, 73.13) * mm});
            skLineSegment(sketch, "E29.4.0.2", {"start": v(-81.25, 73.13) * mm, "end": v(-81.25, 23.13) * mm});
            skLineSegment(sketch, "E29.4.0.3", {"start": v(-83.25, 71.13) * mm, "end": v(-129.25, 71.13) * mm});
            skLineSegment(sketch, "E29.4.0.4", {"start": v(-129.25, 71.13) * mm, "end": v(-129.25, 23.13) * mm});
            skLineSegment(sketch, "E29.4.0.5", {"start": v(-131.25, 73.13) * mm, "end": v(-81.25, 73.13) * mm});
            skLineSegment(sketch, "E29.4.0.6", {"start": v(-81.25, 23.13) * mm, "end": v(-83.25, 23.13) * mm});
            skLineSegment(sketch, "E29.4.0.7", {"start": v(-129.25, 23.13) * mm, "end": v(-131.25, 23.13) * mm});
            skLineSegment(sketch, "E29.5.0.0", {"start": v(146.75, 23.13) * mm, "end": v(146.75, 71.13) * mm});
            skLineSegment(sketch, "E29.5.0.1", {"start": v(98.75, 23.13) * mm, "end": v(98.75, 73.13) * mm});
            skLineSegment(sketch, "E29.5.0.2", {"start": v(148.75, 73.13) * mm, "end": v(148.75, 23.13) * mm});
            skLineSegment(sketch, "E29.5.0.3", {"start": v(146.75, 71.13) * mm, "end": v(100.75, 71.13) * mm});
            skLineSegment(sketch, "E29.5.0.4", {"start": v(100.75, 71.13) * mm, "end": v(100.75, 23.13) * mm});
            skLineSegment(sketch, "E29.5.0.5", {"start": v(98.75, 73.13) * mm, "end": v(148.75, 73.13) * mm});
            skLineSegment(sketch, "E29.5.0.6", {"start": v(148.75, 23.13) * mm, "end": v(146.75, 23.13) * mm});
            skLineSegment(sketch, "E29.5.0.7", {"start": v(100.75, 23.13) * mm, "end": v(98.75, 23.13) * mm});
            skLineSegment(sketch, "E29.6.0.0", {"start": v(376.75, 23.13) * mm, "end": v(376.75, 71.13) * mm});
            skLineSegment(sketch, "E29.6.0.1", {"start": v(328.75, 23.13) * mm, "end": v(328.75, 73.13) * mm});
            skLineSegment(sketch, "E29.6.0.2", {"start": v(378.75, 73.13) * mm, "end": v(378.75, 23.13) * mm});
            skLineSegment(sketch, "E29.6.0.3", {"start": v(376.75, 71.13) * mm, "end": v(330.75, 71.13) * mm});
            skLineSegment(sketch, "E29.6.0.4", {"start": v(330.75, 71.13) * mm, "end": v(330.75, 23.13) * mm});
            skLineSegment(sketch, "E29.6.0.5", {"start": v(328.75, 73.13) * mm, "end": v(378.75, 73.13) * mm});
            skLineSegment(sketch, "E29.6.0.6", {"start": v(378.75, 23.13) * mm, "end": v(376.75, 23.13) * mm});
            skLineSegment(sketch, "E29.6.0.7", {"start": v(330.75, 23.13) * mm, "end": v(328.75, 23.13) * mm});
            skLineSegment(sketch, "E29.7.0.0", {"start": v(606.75, 23.13) * mm, "end": v(606.75, 71.13) * mm});
            skLineSegment(sketch, "E29.7.0.1", {"start": v(558.75, 23.13) * mm, "end": v(558.75, 73.13) * mm});
            skLineSegment(sketch, "E29.7.0.2", {"start": v(608.75, 73.13) * mm, "end": v(608.75, 23.13) * mm});
            skLineSegment(sketch, "E29.7.0.3", {"start": v(606.75, 71.13) * mm, "end": v(560.75, 71.13) * mm});
            skLineSegment(sketch, "E29.7.0.4", {"start": v(560.75, 71.13) * mm, "end": v(560.75, 23.13) * mm});
            skLineSegment(sketch, "E29.7.0.5", {"start": v(558.75, 73.13) * mm, "end": v(608.75, 73.13) * mm});
            skLineSegment(sketch, "E29.7.0.6", {"start": v(608.75, 23.13) * mm, "end": v(606.75, 23.13) * mm});
            skLineSegment(sketch, "E29.7.0.7", {"start": v(560.75, 23.13) * mm, "end": v(558.75, 23.13) * mm});
            skLineSegment(sketch, "E29.8.0.0", {"start": v(836.75, 23.13) * mm, "end": v(836.75, 71.13) * mm});
            skLineSegment(sketch, "E29.8.0.1", {"start": v(788.75, 23.13) * mm, "end": v(788.75, 73.13) * mm});
            skLineSegment(sketch, "E29.8.0.2", {"start": v(838.75, 73.13) * mm, "end": v(838.75, 23.13) * mm});
            skLineSegment(sketch, "E29.8.0.3", {"start": v(836.75, 71.13) * mm, "end": v(790.75, 71.13) * mm});
            skLineSegment(sketch, "E29.8.0.4", {"start": v(790.75, 71.13) * mm, "end": v(790.75, 23.13) * mm});
            skLineSegment(sketch, "E29.8.0.5", {"start": v(788.75, 73.13) * mm, "end": v(838.75, 73.13) * mm});
            skLineSegment(sketch, "E29.8.0.6", {"start": v(838.75, 23.13) * mm, "end": v(836.75, 23.13) * mm});
            skLineSegment(sketch, "E29.8.0.7", {"start": v(790.75, 23.13) * mm, "end": v(788.75, 23.13) * mm});
            skLineSegment(sketch, "E29.9.0.0", {"start": v(1066.75, 23.13) * mm, "end": v(1066.75, 71.13) * mm});
            skLineSegment(sketch, "E29.9.0.1", {"start": v(1018.75, 23.13) * mm, "end": v(1018.75, 73.13) * mm});
            skLineSegment(sketch, "E29.9.0.2", {"start": v(1068.75, 73.13) * mm, "end": v(1068.75, 23.13) * mm});
            skLineSegment(sketch, "E29.9.0.3", {"start": v(1066.75, 71.13) * mm, "end": v(1020.75, 71.13) * mm});
            skLineSegment(sketch, "E29.9.0.4", {"start": v(1020.75, 71.13) * mm, "end": v(1020.75, 23.13) * mm});
            skLineSegment(sketch, "E29.9.0.5", {"start": v(1018.75, 73.13) * mm, "end": v(1068.75, 73.13) * mm});
            skLineSegment(sketch, "E29.9.0.6", {"start": v(1068.75, 23.13) * mm, "end": v(1066.75, 23.13) * mm});
            skLineSegment(sketch, "E29.9.0.7", {"start": v(1020.75, 23.13) * mm, "end": v(1018.75, 23.13) * mm});
            skLineSegment(sketch, "E29.direction1", {"start": v(-1051.25, 23.13) * mm, "end": v(-821.25, 23.13) * mm, "construction": true});
            skSolve(sketch);
        }
        {
            var Q0;
            Q0 = qSketchRegion(id + "F8", true);
            extrude(context, id + "F9", {"entities" : qUnion([Q0]), "operationType" : NewBodyOperationType.ADD, "oppositeDirection" : true, "depth" : 1200 * mm, "offsetDistance" : 25 * mm});
        }
        {
            var Q0;
            Q0=makeQuery(id+"F7.opExtrude","CAP_FACE",FACE,{"disambiguationData":[OSD([sQuery(id+"F6.wireOp",EDGE,"E11.bottom"),sQuery(id+"F6.wireOp",EDGE,"E12.bottom"),sQuery(id+"F6.wireOp",EDGE,"E12.left"),sQuery(id+"F6.wireOp",EDGE,"E12.right"),sQuery(id+"F6.wireOp",EDGE,"E13"),sQuery(id+"F6.wireOp",EDGE,"E14"),sQuery(id+"F6.wireOp",EDGE,"E15"),sQuery(id+"F6.wireOp",EDGE,"E16"),sQuery(id+"F6.wireOp",EDGE,"E17"),sQuery(id+"F6.wireOp",EDGE,"E18"),sQuery(id+"F6.wireOp",EDGE,"E19"),sQuery(id+"F6.wireOp",EDGE,"E20.1.0.0"),sQuery(id+"F6.wireOp",EDGE,"E20.1.0.1"),sQuery(id+"F6.wireOp",EDGE,"E20.1.0.2"),sQuery(id+"F6.wireOp",EDGE,"E20.1.0.3"),sQuery(id+"F6.wireOp",EDGE,"E20.1.0.4"),sQuery(id+"F6.wireOp",EDGE,"E20.1.0.5"),sQuery(id+"F6.wireOp",EDGE,"E20.2.0.0"),sQuery(id+"F6.wireOp",EDGE,"E20.2.0.1"),sQuery(id+"F6.wireOp",EDGE,"E20.2.0.2"),sQuery(id+"F6.wireOp",EDGE,"E20.2.0.3"),sQuery(id+"F6.wireOp",EDGE,"E20.2.0.4"),sQuery(id+"F6.wireOp",EDGE,"E20.2.0.5"),sQuery(id+"F6.wireOp",EDGE,"E20.3.0.0"),sQuery(id+"F6.wireOp",EDGE,"E20.3.0.1"),sQuery(id+"F6.wireOp",EDGE,"E20.3.0.2"),sQuery(id+"F6.wireOp",EDGE,"E20.3.0.3"),sQuery(id+"F6.wireOp",EDGE,"E20.3.0.4"),sQuery(id+"F6.wireOp",EDGE,"E20.3.0.5"),sQuery(id+"F6.wireOp",EDGE,"E20.4.0.0"),sQuery(id+"F6.wireOp",EDGE,"E20.4.0.1"),sQuery(id+"F6.wireOp",EDGE,"E20.4.0.2"),sQuery(id+"F6.wireOp",EDGE,"E20.4.0.3"),sQuery(id+"F6.wireOp",EDGE,"E20.4.0.4"),sQuery(id+"F6.wireOp",EDGE,"E20.4.0.5"),sQuery(id+"F6.wireOp",EDGE,"E20.5.0.0"),sQuery(id+"F6.wireOp",EDGE,"E20.5.0.1"),sQuery(id+"F6.wireOp",EDGE,"E20.5.0.2"),sQuery(id+"F6.wireOp",EDGE,"E20.5.0.3"),sQuery(id+"F6.wireOp",EDGE,"E20.5.0.4"),sQuery(id+"F6.wireOp",EDGE,"E20.5.0.5"),sQuery(id+"F6.wireOp",EDGE,"E20.6.0.0"),sQuery(id+"F6.wireOp",EDGE,"E20.6.0.1"),sQuery(id+"F6.wireOp",EDGE,"E20.6.0.2"),sQuery(id+"F6.wireOp",EDGE,"E20.6.0.3"),sQuery(id+"F6.wireOp",EDGE,"E20.6.0.4"),sQuery(id+"F6.wireOp",EDGE,"E20.6.0.5"),sQuery(id+"F6.wireOp",EDGE,"E20.7.0.0"),sQuery(id+"F6.wireOp",EDGE,"E20.7.0.1"),sQuery(id+"F6.wireOp",EDGE,"E20.7.0.2"),sQuery(id+"F6.wireOp",EDGE,"E20.7.0.3"),sQuery(id+"F6.wireOp",EDGE,"E20.7.0.4"),sQuery(id+"F6.wireOp",EDGE,"E20.7.0.5"),sQuery(id+"F6.wireOp",EDGE,"E20.8.0.0"),sQuery(id+"F6.wireOp",EDGE,"E20.8.0.1"),sQuery(id+"F6.wireOp",EDGE,"E20.8.0.2"),sQuery(id+"F6.wireOp",EDGE,"E20.8.0.3"),sQuery(id+"F6.wireOp",EDGE,"E20.8.0.4"),sQuery(id+"F6.wireOp",EDGE,"E20.8.0.5"),sQuery(id+"F6.wireOp",EDGE,"E20.9.0.0"),sQuery(id+"F6.wireOp",EDGE,"E20.9.0.1"),sQuery(id+"F6.wireOp",EDGE,"E20.9.0.2"),sQuery(id+"F6.wireOp",EDGE,"E20.9.0.3"),sQuery(id+"F6.wireOp",EDGE,"E20.9.0.4"),sQuery(id+"F6.wireOp",EDGE,"E20.9.0.5")])],"isStart":false});
            cPlane(context, id + "F10", {"entities" : qUnion([Q0]), "cplaneType" : CPlaneType.OFFSET, "offset" : 1200 * mm, "oppositeDirection" : true, "width" : 150 * mm, "height" : 150 * mm});
        }
        {
            var Q0;
            Q0=qCreatedBy(id+"F10.planeOp",FACE);
            var sketch = newSketch(context, id + "F11", { "sketchPlane" : qUnion([Q0])});
            skLineSegment(sketch, "E30.bottom", {"start": v(-1246.2, 23.13) * mm, "end": v(1253.8, 23.13) * mm});
            skLineSegment(sketch, "E31.bottom", {"start": v(-1046.2, 73.13) * mm, "end": v(-996.2, 73.13) * mm});
            skLineSegment(sketch, "E31.left", {"start": v(-996.2, 73.13) * mm, "end": v(-996.2, 23.13) * mm});
            skLineSegment(sketch, "E31.right", {"start": v(-1046.2, 73.13) * mm, "end": v(-1046.2, 23.13) * mm});
            skLineSegment(sketch, "E32", {"start": v(-1246.2, 23.13) * mm, "end": v(-1246.2, -26.87) * mm});
            skLineSegment(sketch, "E33", {"start": v(-1246.2, -26.87) * mm, "end": v(5.06, -176.87) * mm});
            skLineSegment(sketch, "E34", {"start": v(5.06, -176.87) * mm, "end": v(1253.8, -26.87) * mm});
            skLineSegment(sketch, "E35", {"start": v(1253.8, -26.87) * mm, "end": v(1253.8, 23.13) * mm});
            skLineSegment(sketch, "E36", {"start": v(-998.2, 23.13) * mm, "end": v(-998.2, 71.13) * mm});
            skLineSegment(sketch, "E37", {"start": v(-998.2, 71.13) * mm, "end": v(-1044.2, 71.13) * mm});
            skLineSegment(sketch, "E38", {"start": v(-1044.2, 71.13) * mm, "end": v(-1044.2, 23.13) * mm});
            skLineSegment(sketch, "E39.1.0.0", {"start": v(-816.2, 73.13) * mm, "end": v(-816.2, 23.13) * mm});
            skLineSegment(sketch, "E39.1.0.1", {"start": v(-768.2, 23.13) * mm, "end": v(-768.2, 71.13) * mm});
            skLineSegment(sketch, "E39.1.0.2", {"start": v(-816.2, 73.13) * mm, "end": v(-766.2, 73.13) * mm});
            skLineSegment(sketch, "E39.1.0.3", {"start": v(-766.2, 73.13) * mm, "end": v(-766.2, 23.13) * mm});
            skLineSegment(sketch, "E39.1.0.4", {"start": v(-768.2, 71.13) * mm, "end": v(-814.2, 71.13) * mm});
            skLineSegment(sketch, "E39.1.0.5", {"start": v(-814.2, 71.13) * mm, "end": v(-814.2, 23.13) * mm});
            skLineSegment(sketch, "E39.2.0.0", {"start": v(-586.2, 73.13) * mm, "end": v(-586.2, 23.13) * mm});
            skLineSegment(sketch, "E39.2.0.1", {"start": v(-538.2, 23.13) * mm, "end": v(-538.2, 71.13) * mm});
            skLineSegment(sketch, "E39.2.0.2", {"start": v(-586.2, 73.13) * mm, "end": v(-536.2, 73.13) * mm});
            skLineSegment(sketch, "E39.2.0.3", {"start": v(-536.2, 73.13) * mm, "end": v(-536.2, 23.13) * mm});
            skLineSegment(sketch, "E39.2.0.4", {"start": v(-538.2, 71.13) * mm, "end": v(-584.2, 71.13) * mm});
            skLineSegment(sketch, "E39.2.0.5", {"start": v(-584.2, 71.13) * mm, "end": v(-584.2, 23.13) * mm});
            skLineSegment(sketch, "E39.3.0.0", {"start": v(-356.2, 73.13) * mm, "end": v(-356.2, 23.13) * mm});
            skLineSegment(sketch, "E39.3.0.1", {"start": v(-308.2, 23.13) * mm, "end": v(-308.2, 71.13) * mm});
            skLineSegment(sketch, "E39.3.0.2", {"start": v(-356.2, 73.13) * mm, "end": v(-306.2, 73.13) * mm});
            skLineSegment(sketch, "E39.3.0.3", {"start": v(-306.2, 73.13) * mm, "end": v(-306.2, 23.13) * mm});
            skLineSegment(sketch, "E39.3.0.4", {"start": v(-308.2, 71.13) * mm, "end": v(-354.2, 71.13) * mm});
            skLineSegment(sketch, "E39.3.0.5", {"start": v(-354.2, 71.13) * mm, "end": v(-354.2, 23.13) * mm});
            skLineSegment(sketch, "E39.4.0.0", {"start": v(-126.2, 73.13) * mm, "end": v(-126.2, 23.13) * mm});
            skLineSegment(sketch, "E39.4.0.1", {"start": v(-78.2, 23.13) * mm, "end": v(-78.2, 71.13) * mm});
            skLineSegment(sketch, "E39.4.0.2", {"start": v(-126.2, 73.13) * mm, "end": v(-76.2, 73.13) * mm});
            skLineSegment(sketch, "E39.4.0.3", {"start": v(-76.2, 73.13) * mm, "end": v(-76.2, 23.13) * mm});
            skLineSegment(sketch, "E39.4.0.4", {"start": v(-78.2, 71.13) * mm, "end": v(-124.2, 71.13) * mm});
            skLineSegment(sketch, "E39.4.0.5", {"start": v(-124.2, 71.13) * mm, "end": v(-124.2, 23.13) * mm});
            skLineSegment(sketch, "E39.5.0.0", {"start": v(103.8, 73.13) * mm, "end": v(103.8, 23.13) * mm});
            skLineSegment(sketch, "E39.5.0.1", {"start": v(151.8, 23.13) * mm, "end": v(151.8, 71.13) * mm});
            skLineSegment(sketch, "E39.5.0.2", {"start": v(103.8, 73.13) * mm, "end": v(153.8, 73.13) * mm});
            skLineSegment(sketch, "E39.5.0.3", {"start": v(153.8, 73.13) * mm, "end": v(153.8, 23.13) * mm});
            skLineSegment(sketch, "E39.5.0.4", {"start": v(151.8, 71.13) * mm, "end": v(105.8, 71.13) * mm});
            skLineSegment(sketch, "E39.5.0.5", {"start": v(105.8, 71.13) * mm, "end": v(105.8, 23.13) * mm});
            skLineSegment(sketch, "E39.6.0.0", {"start": v(333.8, 73.13) * mm, "end": v(333.8, 23.13) * mm});
            skLineSegment(sketch, "E39.6.0.1", {"start": v(381.8, 23.13) * mm, "end": v(381.8, 71.13) * mm});
            skLineSegment(sketch, "E39.6.0.2", {"start": v(333.8, 73.13) * mm, "end": v(383.8, 73.13) * mm});
            skLineSegment(sketch, "E39.6.0.3", {"start": v(383.8, 73.13) * mm, "end": v(383.8, 23.13) * mm});
            skLineSegment(sketch, "E39.6.0.4", {"start": v(381.8, 71.13) * mm, "end": v(335.8, 71.13) * mm});
            skLineSegment(sketch, "E39.6.0.5", {"start": v(335.8, 71.13) * mm, "end": v(335.8, 23.13) * mm});
            skLineSegment(sketch, "E39.7.0.0", {"start": v(563.8, 73.13) * mm, "end": v(563.8, 23.13) * mm});
            skLineSegment(sketch, "E39.7.0.1", {"start": v(611.8, 23.13) * mm, "end": v(611.8, 71.13) * mm});
            skLineSegment(sketch, "E39.7.0.2", {"start": v(563.8, 73.13) * mm, "end": v(613.8, 73.13) * mm});
            skLineSegment(sketch, "E39.7.0.3", {"start": v(613.8, 73.13) * mm, "end": v(613.8, 23.13) * mm});
            skLineSegment(sketch, "E39.7.0.4", {"start": v(611.8, 71.13) * mm, "end": v(565.8, 71.13) * mm});
            skLineSegment(sketch, "E39.7.0.5", {"start": v(565.8, 71.13) * mm, "end": v(565.8, 23.13) * mm});
            skLineSegment(sketch, "E39.8.0.0", {"start": v(793.8, 73.13) * mm, "end": v(793.8, 23.13) * mm});
            skLineSegment(sketch, "E39.8.0.1", {"start": v(841.8, 23.13) * mm, "end": v(841.8, 71.13) * mm});
            skLineSegment(sketch, "E39.8.0.2", {"start": v(793.8, 73.13) * mm, "end": v(843.8, 73.13) * mm});
            skLineSegment(sketch, "E39.8.0.3", {"start": v(843.8, 73.13) * mm, "end": v(843.8, 23.13) * mm});
            skLineSegment(sketch, "E39.8.0.4", {"start": v(841.8, 71.13) * mm, "end": v(795.8, 71.13) * mm});
            skLineSegment(sketch, "E39.8.0.5", {"start": v(795.8, 71.13) * mm, "end": v(795.8, 23.13) * mm});
            skLineSegment(sketch, "E39.9.0.0", {"start": v(1023.8, 73.13) * mm, "end": v(1023.8, 23.13) * mm});
            skLineSegment(sketch, "E39.9.0.1", {"start": v(1071.8, 23.13) * mm, "end": v(1071.8, 71.13) * mm});
            skLineSegment(sketch, "E39.9.0.2", {"start": v(1023.8, 73.13) * mm, "end": v(1073.8, 73.13) * mm});
            skLineSegment(sketch, "E39.9.0.3", {"start": v(1073.8, 73.13) * mm, "end": v(1073.8, 23.13) * mm});
            skLineSegment(sketch, "E39.9.0.4", {"start": v(1071.8, 71.13) * mm, "end": v(1025.8, 71.13) * mm});
            skLineSegment(sketch, "E39.9.0.5", {"start": v(1025.8, 71.13) * mm, "end": v(1025.8, 23.13) * mm});
            skLineSegment(sketch, "E39.direction1", {"start": v(-1046.2, 23.13) * mm, "end": v(-816.2, 23.13) * mm, "construction": true});
            skSolve(sketch);
        }
        {
            var Q0;
            Q0 = qSketchRegion(id + "F11", true);
            extrude(context, id + "F12", {"entities" : qUnion([Q0]), "depth" : 3 * mm, "offsetDistance" : 25 * mm});
        }
    });
